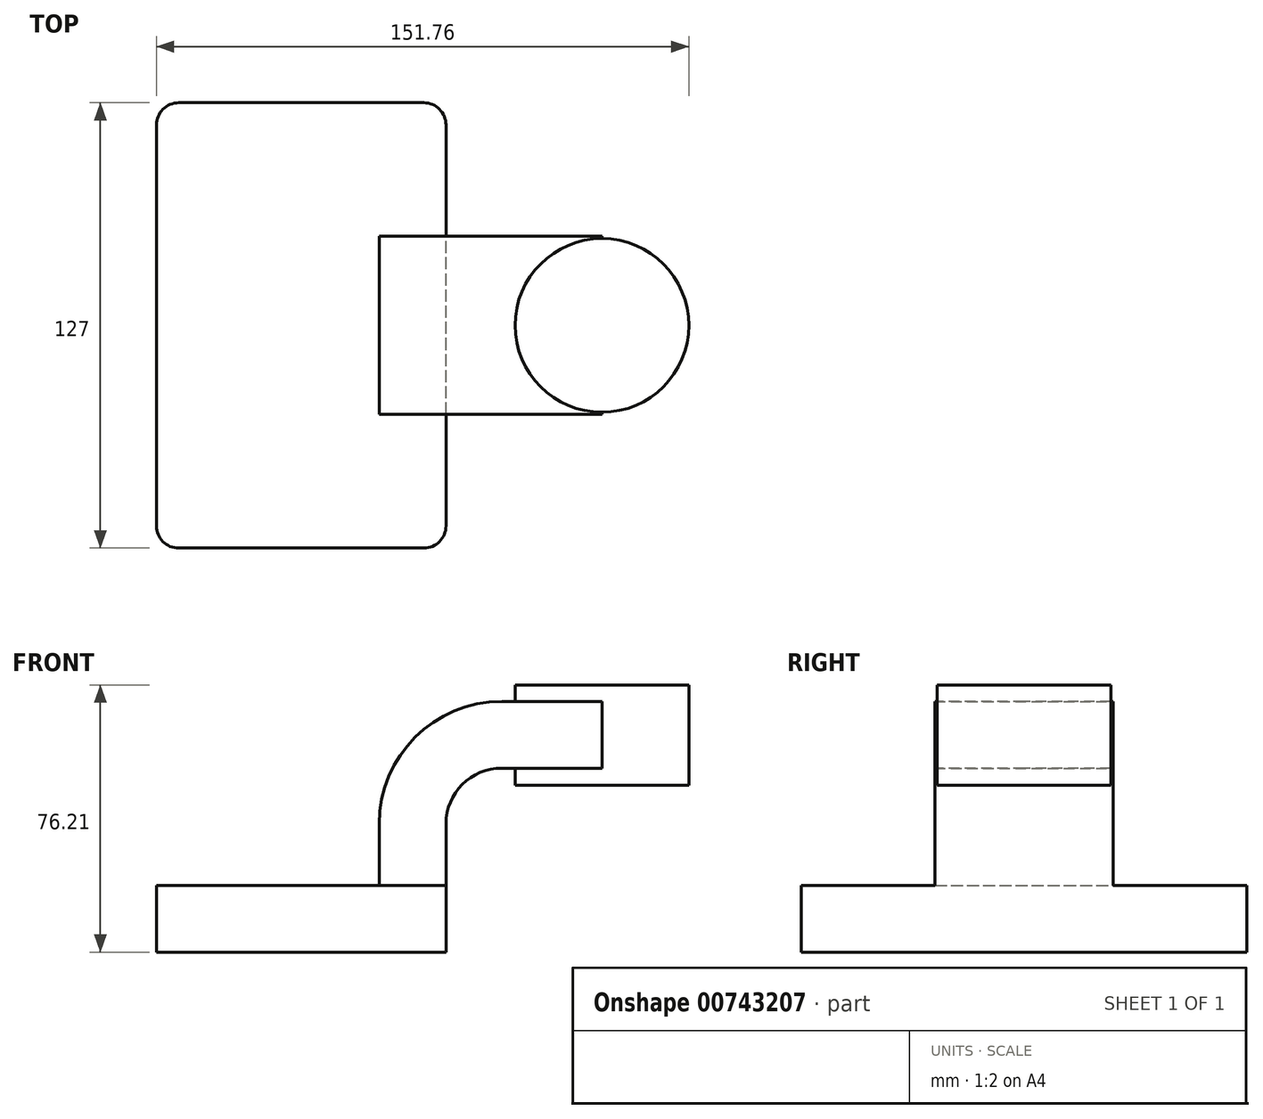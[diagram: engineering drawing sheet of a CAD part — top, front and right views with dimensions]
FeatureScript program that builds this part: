
annotation { "Feature Type Name" : "Feature", "Feature Type Description" : "" }
export const myFeature = defineFeature(function(context is Context, id is Id, definition is map)
    precondition{}
    {
        {
            var Q0;
            Q0=qCreatedBy(makeId("Front.planeOp"),FACE);
            var sketch = newSketch(context, id + "F0", { "sketchPlane" : qUnion([Q0])});
            skLineSegment(sketch, "E0.bottom", {"start": v(-41.28, -9.53) * mm, "end": v(41.28, -9.53) * mm});
            skLineSegment(sketch, "E0.top", {"start": v(-41.28, 9.52) * mm, "end": v(41.28, 9.52) * mm});
            skLineSegment(sketch, "E0.left", {"start": v(-41.28, -9.53) * mm, "end": v(-41.28, 9.52) * mm});
            skLineSegment(sketch, "E0.right", {"start": v(41.28, -9.53) * mm, "end": v(41.28, 9.52) * mm});
            skPoint(sketch, "E0.middle", {"position": v(0, 0) * mm});
            skLineSegment(sketch, "E1.bottom", {"start": v(59.69, 38.1) * mm, "end": v(110.49, 38.1) * mm});
            skLineSegment(sketch, "E1.top", {"start": v(59.69, 66.68) * mm, "end": v(110.49, 66.68) * mm});
            skLineSegment(sketch, "E1.left", {"start": v(59.69, 38.1) * mm, "end": v(59.69, 66.68) * mm});
            skLineSegment(sketch, "E1.right", {"start": v(110.49, 38.1) * mm, "end": v(110.49, 66.68) * mm});
            skPoint(sketch, "E1.middle", {"position": v(85.09, 52.39) * mm});
            skLineSegment(sketch, "E2", {"start": v(41.28, 9.52) * mm, "end": v(41.28, 27.05) * mm});
            skArc(sketch, "E3", {"start": v(41.27, 27.05) * mm, "mid": v(45.92, 38.28) * mm, "end": v(57.15, 42.93) * mm});
            skLineSegment(sketch, "E4", {"start": v(57.15, 42.93) * mm, "end": v(85.72, 42.93) * mm});
            skLineSegment(sketch, "E5.0", {"start": v(57.15, 61.98) * mm, "end": v(85.72, 61.98) * mm});
            skArc(sketch, "E5.1", {"start": v(22.22, 27.05) * mm, "mid": v(32.45, 51.75) * mm, "end": v(57.15, 61.98) * mm});
            skLineSegment(sketch, "E5.2", {"start": v(22.22, 9.52) * mm, "end": v(22.22, 27.05) * mm});
            skLineSegment(sketch, "E6", {"start": v(85.72, 38.1) * mm, "end": v(85.72, 66.68) * mm});
            skFitSpline(sketch, "E7", {"points": [v(-41.28, 9.53) * mm, v(57.15, 61.98) * mm], "startDerivative": vector(0.68, 92.86) * mm, "endDerivative": vector(158.4, -0.2) * mm});
            skSolve(sketch);
        }
        {
            var Q0;
            Q0=makeQuery(id+"F0.imprint","IMPRINT",FACE,{"disambiguationData":[TD([[makeQuery(id+"F0.imprint","IMPRINT",EDGE,{"derivedFrom":sQuery(id+"F0.wireOp",EDGE,"E0.bottom")}),1.0]])]});
            extrude(context, id + "F1", {"entities" : qUnion([Q0]), "endBound" : BoundingType.SYMMETRIC, "depth" : 127 * mm, "offsetDistance" : 25.4 * mm});
        }
        {
            var Q0;
            {var subQ0=sQuery(id+"F0.wireOp",EDGE,"E4");var subQ1=sQuery(id+"F0.wireOp",EDGE,"E1.left");var subQ2=makeQuery(id+"F0.imprint","INTERSECT",VERTEX,{"derivedFrom":[subQ1,subQ0]});Q0=makeQuery(id+"F0.imprint","IMPRINT",FACE,{"disambiguationData":[TD([[makeQuery(id+"F0.imprint","IMPRINT",EDGE,{"disambiguationData":[TD([[subQ2,-1.0]])],"derivedFrom":subQ1}),-1.0]])]});}
            var Q1;
            {var subQ1=sQuery(id+"F0.wireOp",EDGE,"E2");Q1=makeQuery(id+"F0.imprint","IMPRINT",FACE,{"disambiguationData":[TD([[makeQuery(id+"F0.imprint","IMPRINT",EDGE,{"derivedFrom":subQ1}),1.0]])]});}
            extrude(context, id + "F2", {"entities" : qUnion([Q0, Q1]), "operationType" : NewBodyOperationType.ADD, "endBound" : BoundingType.SYMMETRIC, "depth" : 50.8 * mm, "offsetDistance" : 25.4 * mm});
        }
        {
            var Q0;
            Q0=makeQuery(id+"F0.imprint","IMPRINT",FACE,{"disambiguationData":[TD([[makeQuery(id+"F0.imprint","IMPRINT",EDGE,{"derivedFrom":sQuery(id+"F0.wireOp",EDGE,"E5.1")}),1.0]])]});
            extrude(context, id + "F3", {"entities" : qUnion([Q0]), "operationType" : NewBodyOperationType.ADD, "endBound" : BoundingType.SYMMETRIC, "depth" : 15.88 * mm, "offsetDistance" : 25.4 * mm});
        }
        {
            var Q0;
            {var subQ4=sQuery(id+"F0.wireOp",EDGE,"E1.right");Q0=makeQuery(id+"F0.imprint","IMPRINT",FACE,{"disambiguationData":[TD([[makeQuery(id+"F0.imprint","IMPRINT",EDGE,{"derivedFrom":subQ4}),1.0]])]});}
            var Q1;
            Q1=sQuery(id+"F0.wireOp",EDGE,"E6");
            revolve(context, id + "F4", {"operationType" : NewBodyOperationType.ADD, "surfaceOperationType" : NewSurfaceOperationType.NEW, "entities" : qUnion([Q0]), "axis" : qUnion([Q1]), "revolveType" : RevolveType.FULL});
        }
        {
            var Q0;
            Q0=makeQuery(id+"F1.opExtrude","CAP_EDGE",EDGE,{"disambiguationData":[OSD([sQuery(id+"F0.wireOp",EDGE,"E0.right")])],"isStart":false});
            var Q1;
            Q1=makeQuery(id+"F1.opExtrude","CAP_EDGE",EDGE,{"disambiguationData":[OSD([sQuery(id+"F0.wireOp",EDGE,"E0.left")])],"isStart":false});
            var Q2;
            Q2=makeQuery(id+"F1.opExtrude","CAP_EDGE",EDGE,{"disambiguationData":[OSD([sQuery(id+"F0.wireOp",EDGE,"E0.left")])],"isStart":true});
            var Q3;
            Q3=makeQuery(id+"F1.opExtrude","CAP_EDGE",EDGE,{"disambiguationData":[OSD([sQuery(id+"F0.wireOp",EDGE,"E0.right")])],"isStart":true});
            fillet(context, id + "F5", {"entities" : qUnion([Q0, Q1, Q2, Q3]), "radius" : 6.35 * mm, "tangentPropagation" : true, "allowEdgeOverflow" : false});
        }
    });
